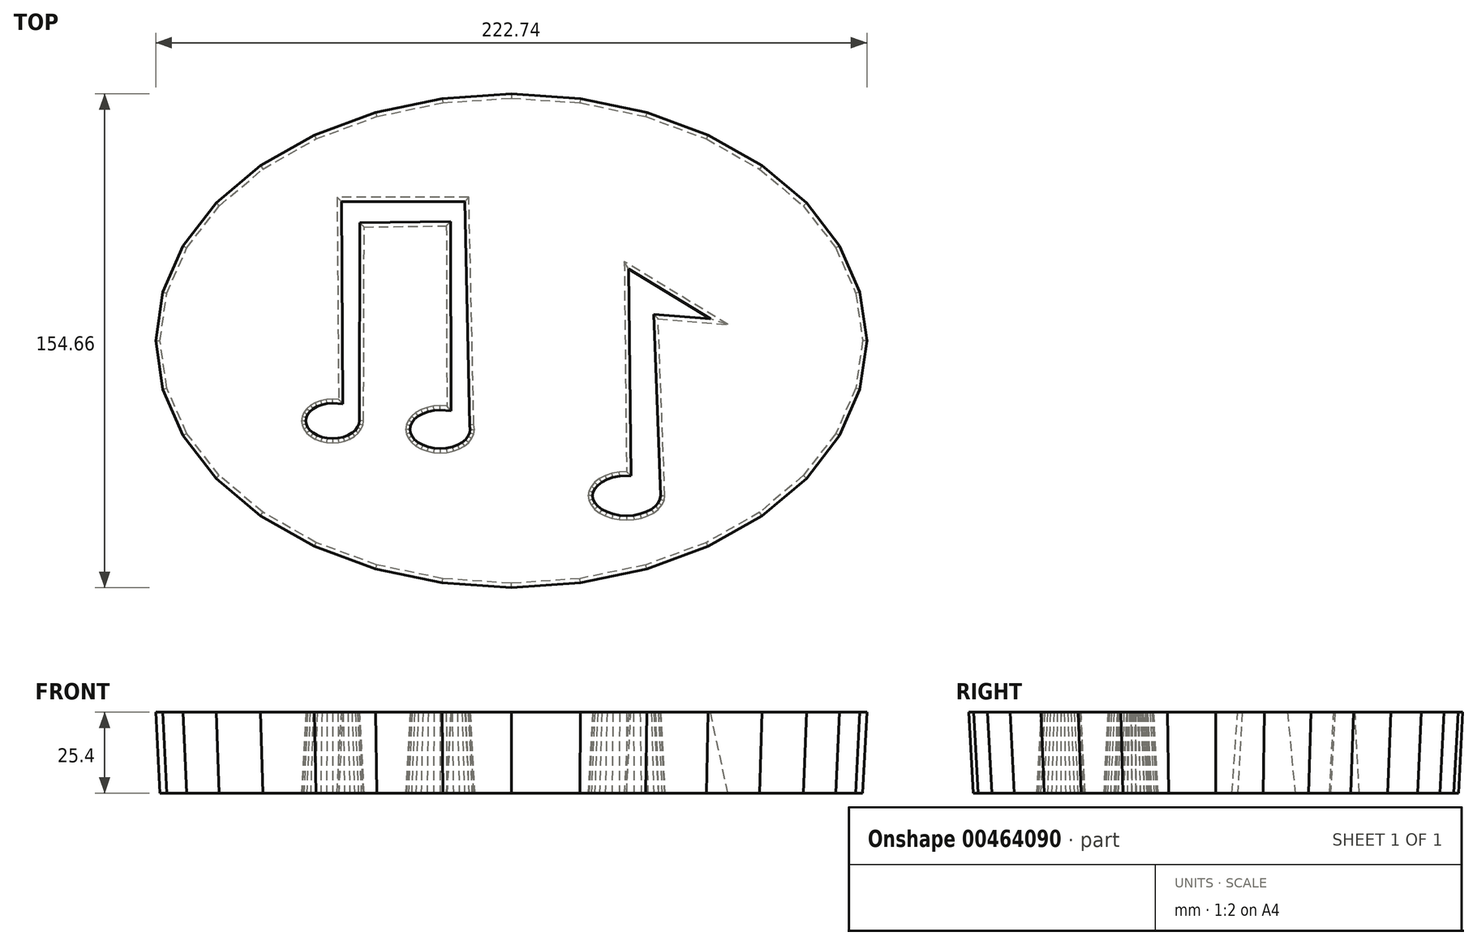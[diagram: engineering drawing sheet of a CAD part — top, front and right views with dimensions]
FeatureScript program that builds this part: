
annotation { "Feature Type Name" : "Feature", "Feature Type Description" : "" }
export const myFeature = defineFeature(function(context is Context, id is Id, definition is map)
    precondition{}
    {
        {
            var Q0;
            Q0=qCreatedBy(makeId("Top.planeOp"),FACE);
            var sketch = newSketch(context, id + "F0", { "sketchPlane" : qUnion([Q0])});
            skLineSegment(sketch, "E0", {"start": v(110.03, 0) * mm, "end": v(107.91, 14.83) * mm});
            skLineSegment(sketch, "E1", {"start": v(107.91, 14.83) * mm, "end": v(101.65, 29.08) * mm});
            skLineSegment(sketch, "E2", {"start": v(101.65, 29.08) * mm, "end": v(91.48, 42.22) * mm});
            skLineSegment(sketch, "E3", {"start": v(91.48, 42.22) * mm, "end": v(77.8, 53.74) * mm});
            skLineSegment(sketch, "E4", {"start": v(77.8, 53.74) * mm, "end": v(61.13, 63.19) * mm});
            skLineSegment(sketch, "E5", {"start": v(61.13, 63.19) * mm, "end": v(42.1, 70.2) * mm});
            skLineSegment(sketch, "E6", {"start": v(42.1, 70.2) * mm, "end": v(21.47, 74.53) * mm});
            skLineSegment(sketch, "E7", {"start": v(21.47, 74.53) * mm, "end": v(0, 76) * mm});
            skLineSegment(sketch, "E8", {"start": v(0, 76) * mm, "end": v(-21.47, 74.53) * mm});
            skLineSegment(sketch, "E9", {"start": v(-21.47, 74.53) * mm, "end": v(-42.1, 70.2) * mm});
            skLineSegment(sketch, "E10", {"start": v(-42.1, 70.2) * mm, "end": v(-61.13, 63.19) * mm});
            skLineSegment(sketch, "E11", {"start": v(-61.13, 63.19) * mm, "end": v(-77.8, 53.74) * mm});
            skLineSegment(sketch, "E12", {"start": v(-77.8, 53.74) * mm, "end": v(-91.48, 42.22) * mm});
            skLineSegment(sketch, "E13", {"start": v(-91.48, 42.22) * mm, "end": v(-101.65, 29.08) * mm});
            skLineSegment(sketch, "E14", {"start": v(-101.65, 29.08) * mm, "end": v(-107.91, 14.83) * mm});
            skLineSegment(sketch, "E15", {"start": v(-107.91, 14.83) * mm, "end": v(-110.03, 0) * mm});
            skLineSegment(sketch, "E16", {"start": v(-110.03, 0) * mm, "end": v(-107.91, -14.83) * mm});
            skLineSegment(sketch, "E17", {"start": v(-107.91, -14.83) * mm, "end": v(-101.65, -29.08) * mm});
            skLineSegment(sketch, "E18", {"start": v(-101.65, -29.08) * mm, "end": v(-91.48, -42.22) * mm});
            skLineSegment(sketch, "E19", {"start": v(-91.48, -42.22) * mm, "end": v(-77.8, -53.74) * mm});
            skLineSegment(sketch, "E20", {"start": v(-77.8, -53.74) * mm, "end": v(-61.13, -63.19) * mm});
            skLineSegment(sketch, "E21", {"start": v(-61.13, -63.19) * mm, "end": v(-42.1, -70.2) * mm});
            skLineSegment(sketch, "E22", {"start": v(-42.1, -70.2) * mm, "end": v(-21.47, -74.53) * mm});
            skLineSegment(sketch, "E23", {"start": v(-21.47, -74.53) * mm, "end": v(0, -76) * mm});
            skLineSegment(sketch, "E24", {"start": v(0, -76) * mm, "end": v(21.47, -74.53) * mm});
            skLineSegment(sketch, "E25", {"start": v(21.47, -74.53) * mm, "end": v(42.1, -70.2) * mm});
            skLineSegment(sketch, "E26", {"start": v(42.1, -70.2) * mm, "end": v(61.13, -63.19) * mm});
            skLineSegment(sketch, "E27", {"start": v(61.13, -63.19) * mm, "end": v(77.8, -53.74) * mm});
            skLineSegment(sketch, "E28", {"start": v(77.8, -53.74) * mm, "end": v(91.48, -42.22) * mm});
            skLineSegment(sketch, "E29", {"start": v(91.48, -42.22) * mm, "end": v(101.65, -29.08) * mm});
            skLineSegment(sketch, "E30", {"start": v(101.65, -29.08) * mm, "end": v(107.91, -14.83) * mm});
            skLineSegment(sketch, "E31", {"start": v(107.91, -14.83) * mm, "end": v(110.03, 0) * mm});
            skLineSegment(sketch, "E32", {"start": v(-46.26, -25.1) * mm, "end": v(-46.45, -23.77) * mm});
            skLineSegment(sketch, "E33", {"start": v(-46.45, -23.77) * mm, "end": v(-47, -22.48) * mm});
            skLineSegment(sketch, "E34", {"start": v(-47, -22.48) * mm, "end": v(-47.9, -21.29) * mm});
            skLineSegment(sketch, "E35", {"start": v(-47.9, -21.29) * mm, "end": v(-49.1, -20.24) * mm});
            skLineSegment(sketch, "E36", {"start": v(-49.1, -20.24) * mm, "end": v(-50.58, -19.39) * mm});
            skLineSegment(sketch, "E37", {"start": v(-50.58, -19.39) * mm, "end": v(-52.26, -18.75) * mm});
            skLineSegment(sketch, "E38", {"start": v(-52.26, -18.75) * mm, "end": v(-54.08, -18.36) * mm});
            skLineSegment(sketch, "E39", {"start": v(-54.08, -18.36) * mm, "end": v(-55.98, -18.23) * mm});
            skLineSegment(sketch, "E40", {"start": v(-55.98, -18.23) * mm, "end": v(-57.87, -18.36) * mm});
            skLineSegment(sketch, "E41", {"start": v(-57.87, -18.36) * mm, "end": v(-59.7, -18.75) * mm});
            skLineSegment(sketch, "E42", {"start": v(-59.7, -18.75) * mm, "end": v(-61.37, -19.39) * mm});
            skLineSegment(sketch, "E43", {"start": v(-61.37, -19.39) * mm, "end": v(-62.84, -20.24) * mm});
            skLineSegment(sketch, "E44", {"start": v(-62.84, -20.24) * mm, "end": v(-64.05, -21.29) * mm});
            skLineSegment(sketch, "E45", {"start": v(-64.05, -21.29) * mm, "end": v(-64.95, -22.48) * mm});
            skLineSegment(sketch, "E46", {"start": v(-64.95, -22.48) * mm, "end": v(-65.5, -23.77) * mm});
            skLineSegment(sketch, "E47", {"start": v(-65.5, -23.77) * mm, "end": v(-65.69, -25.1) * mm});
            skLineSegment(sketch, "E48", {"start": v(-65.69, -25.1) * mm, "end": v(-65.5, -26.45) * mm});
            skLineSegment(sketch, "E49", {"start": v(-65.5, -26.45) * mm, "end": v(-64.95, -27.74) * mm});
            skLineSegment(sketch, "E50", {"start": v(-64.95, -27.74) * mm, "end": v(-64.05, -28.93) * mm});
            skLineSegment(sketch, "E51", {"start": v(-64.05, -28.93) * mm, "end": v(-62.84, -29.97) * mm});
            skLineSegment(sketch, "E52", {"start": v(-62.84, -29.97) * mm, "end": v(-61.37, -30.83) * mm});
            skLineSegment(sketch, "E53", {"start": v(-61.37, -30.83) * mm, "end": v(-59.7, -31.46) * mm});
            skLineSegment(sketch, "E54", {"start": v(-59.7, -31.46) * mm, "end": v(-57.87, -31.86) * mm});
            skLineSegment(sketch, "E55", {"start": v(-57.87, -31.86) * mm, "end": v(-55.98, -31.99) * mm});
            skLineSegment(sketch, "E56", {"start": v(-55.98, -31.99) * mm, "end": v(-54.08, -31.86) * mm});
            skLineSegment(sketch, "E57", {"start": v(-54.08, -31.86) * mm, "end": v(-52.26, -31.46) * mm});
            skLineSegment(sketch, "E58", {"start": v(-52.26, -31.46) * mm, "end": v(-50.58, -30.83) * mm});
            skLineSegment(sketch, "E59", {"start": v(-50.58, -30.83) * mm, "end": v(-49.1, -29.97) * mm});
            skLineSegment(sketch, "E60", {"start": v(-49.1, -29.97) * mm, "end": v(-47.9, -28.93) * mm});
            skLineSegment(sketch, "E61", {"start": v(-47.9, -28.93) * mm, "end": v(-47, -27.74) * mm});
            skLineSegment(sketch, "E62", {"start": v(-47, -27.74) * mm, "end": v(-46.45, -26.45) * mm});
            skLineSegment(sketch, "E63", {"start": v(-46.45, -26.45) * mm, "end": v(-46.26, -25.1) * mm});
            skLineSegment(sketch, "E64", {"start": v(-11.51, -27.75) * mm, "end": v(-11.72, -26.3) * mm});
            skLineSegment(sketch, "E65", {"start": v(-11.72, -26.3) * mm, "end": v(-12.33, -24.92) * mm});
            skLineSegment(sketch, "E66", {"start": v(-12.33, -24.92) * mm, "end": v(-13.33, -23.64) * mm});
            skLineSegment(sketch, "E67", {"start": v(-13.33, -23.64) * mm, "end": v(-14.67, -22.52) * mm});
            skLineSegment(sketch, "E68", {"start": v(-14.67, -22.52) * mm, "end": v(-16.3, -21.6) * mm});
            skLineSegment(sketch, "E69", {"start": v(-16.3, -21.6) * mm, "end": v(-18.16, -20.91) * mm});
            skLineSegment(sketch, "E70", {"start": v(-18.16, -20.91) * mm, "end": v(-20.18, -20.49) * mm});
            skLineSegment(sketch, "E71", {"start": v(-20.18, -20.49) * mm, "end": v(-22.27, -20.35) * mm});
            skLineSegment(sketch, "E72", {"start": v(-22.27, -20.35) * mm, "end": v(-24.37, -20.49) * mm});
            skLineSegment(sketch, "E73", {"start": v(-24.37, -20.49) * mm, "end": v(-26.4, -20.91) * mm});
            skLineSegment(sketch, "E74", {"start": v(-26.4, -20.91) * mm, "end": v(-28.25, -21.6) * mm});
            skLineSegment(sketch, "E75", {"start": v(-28.25, -21.6) * mm, "end": v(-29.88, -22.52) * mm});
            skLineSegment(sketch, "E76", {"start": v(-29.88, -22.52) * mm, "end": v(-31.22, -23.64) * mm});
            skLineSegment(sketch, "E77", {"start": v(-31.22, -23.64) * mm, "end": v(-32.22, -24.92) * mm});
            skLineSegment(sketch, "E78", {"start": v(-32.22, -24.92) * mm, "end": v(-32.83, -26.3) * mm});
            skLineSegment(sketch, "E79", {"start": v(-32.83, -26.3) * mm, "end": v(-33.03, -27.75) * mm});
            skLineSegment(sketch, "E80", {"start": v(-33.03, -27.75) * mm, "end": v(-32.83, -29.2) * mm});
            skLineSegment(sketch, "E81", {"start": v(-32.83, -29.2) * mm, "end": v(-32.22, -30.59) * mm});
            skLineSegment(sketch, "E82", {"start": v(-32.22, -30.59) * mm, "end": v(-31.22, -31.87) * mm});
            skLineSegment(sketch, "E83", {"start": v(-31.22, -31.87) * mm, "end": v(-29.88, -33) * mm});
            skLineSegment(sketch, "E84", {"start": v(-29.88, -33) * mm, "end": v(-28.25, -33.91) * mm});
            skLineSegment(sketch, "E85", {"start": v(-28.25, -33.91) * mm, "end": v(-26.4, -34.6) * mm});
            skLineSegment(sketch, "E86", {"start": v(-26.4, -34.6) * mm, "end": v(-24.37, -35.02) * mm});
            skLineSegment(sketch, "E87", {"start": v(-24.37, -35.02) * mm, "end": v(-22.27, -35.16) * mm});
            skLineSegment(sketch, "E88", {"start": v(-22.27, -35.16) * mm, "end": v(-20.18, -35.02) * mm});
            skLineSegment(sketch, "E89", {"start": v(-20.18, -35.02) * mm, "end": v(-18.16, -34.6) * mm});
            skLineSegment(sketch, "E90", {"start": v(-18.16, -34.6) * mm, "end": v(-16.3, -33.91) * mm});
            skLineSegment(sketch, "E91", {"start": v(-16.3, -33.91) * mm, "end": v(-14.67, -33) * mm});
            skLineSegment(sketch, "E92", {"start": v(-14.67, -33) * mm, "end": v(-13.33, -31.87) * mm});
            skLineSegment(sketch, "E93", {"start": v(-13.33, -31.87) * mm, "end": v(-12.33, -30.59) * mm});
            skLineSegment(sketch, "E94", {"start": v(-12.33, -30.59) * mm, "end": v(-11.72, -29.2) * mm});
            skLineSegment(sketch, "E95", {"start": v(-11.72, -29.2) * mm, "end": v(-11.51, -27.75) * mm});
            skLineSegment(sketch, "E96", {"start": v(48.1, -48.57) * mm, "end": v(47.87, -47.09) * mm});
            skLineSegment(sketch, "E97", {"start": v(47.87, -47.09) * mm, "end": v(47.2, -45.67) * mm});
            skLineSegment(sketch, "E98", {"start": v(47.2, -45.67) * mm, "end": v(46.08, -44.35) * mm});
            skLineSegment(sketch, "E99", {"start": v(46.08, -44.35) * mm, "end": v(44.6, -43.2) * mm});
            skLineSegment(sketch, "E100", {"start": v(44.6, -43.2) * mm, "end": v(42.77, -42.26) * mm});
            skLineSegment(sketch, "E101", {"start": v(42.77, -42.26) * mm, "end": v(40.7, -41.56) * mm});
            skLineSegment(sketch, "E102", {"start": v(40.7, -41.56) * mm, "end": v(38.45, -41.13) * mm});
            skLineSegment(sketch, "E103", {"start": v(38.45, -41.13) * mm, "end": v(36.11, -40.98) * mm});
            skLineSegment(sketch, "E104", {"start": v(36.11, -40.98) * mm, "end": v(33.77, -41.13) * mm});
            skLineSegment(sketch, "E105", {"start": v(33.77, -41.13) * mm, "end": v(31.52, -41.56) * mm});
            skLineSegment(sketch, "E106", {"start": v(31.52, -41.56) * mm, "end": v(29.45, -42.26) * mm});
            skLineSegment(sketch, "E107", {"start": v(29.45, -42.26) * mm, "end": v(27.63, -43.2) * mm});
            skLineSegment(sketch, "E108", {"start": v(27.63, -43.2) * mm, "end": v(26.14, -44.35) * mm});
            skLineSegment(sketch, "E109", {"start": v(26.14, -44.35) * mm, "end": v(25.03, -45.67) * mm});
            skLineSegment(sketch, "E110", {"start": v(25.03, -45.67) * mm, "end": v(24.35, -47.09) * mm});
            skLineSegment(sketch, "E111", {"start": v(24.35, -47.09) * mm, "end": v(24.12, -48.57) * mm});
            skLineSegment(sketch, "E112", {"start": v(24.12, -48.57) * mm, "end": v(24.35, -50.05) * mm});
            skLineSegment(sketch, "E113", {"start": v(24.35, -50.05) * mm, "end": v(25.03, -51.47) * mm});
            skLineSegment(sketch, "E114", {"start": v(25.03, -51.47) * mm, "end": v(26.14, -52.78) * mm});
            skLineSegment(sketch, "E115", {"start": v(26.14, -52.78) * mm, "end": v(27.63, -53.93) * mm});
            skLineSegment(sketch, "E116", {"start": v(27.63, -53.93) * mm, "end": v(29.45, -54.87) * mm});
            skLineSegment(sketch, "E117", {"start": v(29.45, -54.87) * mm, "end": v(31.52, -55.58) * mm});
            skLineSegment(sketch, "E118", {"start": v(31.52, -55.58) * mm, "end": v(33.77, -56) * mm});
            skLineSegment(sketch, "E119", {"start": v(33.77, -56) * mm, "end": v(36.11, -56.15) * mm});
            skLineSegment(sketch, "E120", {"start": v(36.11, -56.15) * mm, "end": v(38.45, -56) * mm});
            skLineSegment(sketch, "E121", {"start": v(38.45, -56) * mm, "end": v(40.7, -55.58) * mm});
            skLineSegment(sketch, "E122", {"start": v(40.7, -55.58) * mm, "end": v(42.77, -54.87) * mm});
            skLineSegment(sketch, "E123", {"start": v(42.77, -54.87) * mm, "end": v(44.6, -53.93) * mm});
            skLineSegment(sketch, "E124", {"start": v(44.6, -53.93) * mm, "end": v(46.08, -52.78) * mm});
            skLineSegment(sketch, "E125", {"start": v(46.08, -52.78) * mm, "end": v(47.2, -51.47) * mm});
            skLineSegment(sketch, "E126", {"start": v(47.2, -51.47) * mm, "end": v(47.87, -50.05) * mm});
            skLineSegment(sketch, "E127", {"start": v(47.87, -50.05) * mm, "end": v(48.1, -48.57) * mm});
            skLineSegment(sketch, "E128", {"start": v(36.11, -40.98) * mm, "end": v(35.4, 24.8) * mm});
            skLineSegment(sketch, "E129", {"start": v(35.4, 24.8) * mm, "end": v(67.86, 5.05) * mm});
            skLineSegment(sketch, "E130", {"start": v(48.1, -48.57) * mm, "end": v(45.99, 6.82) * mm});
            skLineSegment(sketch, "E131", {"start": v(45.99, 6.82) * mm, "end": v(67.86, 5.05) * mm});
            skLineSegment(sketch, "E132", {"start": v(-54.55, 44.92) * mm, "end": v(-13.28, 44.92) * mm});
            skLineSegment(sketch, "E133", {"start": v(-54.55, 44.92) * mm, "end": v(-54.08, -18.36) * mm});
            skLineSegment(sketch, "E134", {"start": v(-46.09, 35.6) * mm, "end": v(-20.33, 35.95) * mm});
            skLineSegment(sketch, "E135", {"start": v(-13.28, 44.92) * mm, "end": v(-11.72, -26.3) * mm});
            skLineSegment(sketch, "E136", {"start": v(-20.33, 35.95) * mm, "end": v(-20.18, -20.49) * mm});
            skLineSegment(sketch, "E137", {"start": v(-46.09, 35.6) * mm, "end": v(-46.26, -25.1) * mm});
            skSolve(sketch);
        }
        {
            var Q0;
            Q0=makeQuery(id+"F0.imprint","IMPRINT",FACE,{"disambiguationData":[TD([[makeQuery(id+"F0.imprint","IMPRINT",EDGE,{"derivedFrom":sQuery(id+"F0.wireOp",EDGE,"E0")}),1.0]])]});
            extrude(context, id + "F1", {"entities" : qUnion([Q0]), "depth" : 25.4 * mm, "hasDraft" : true, "draftAngle" : 3 * degree});
        }
    });
